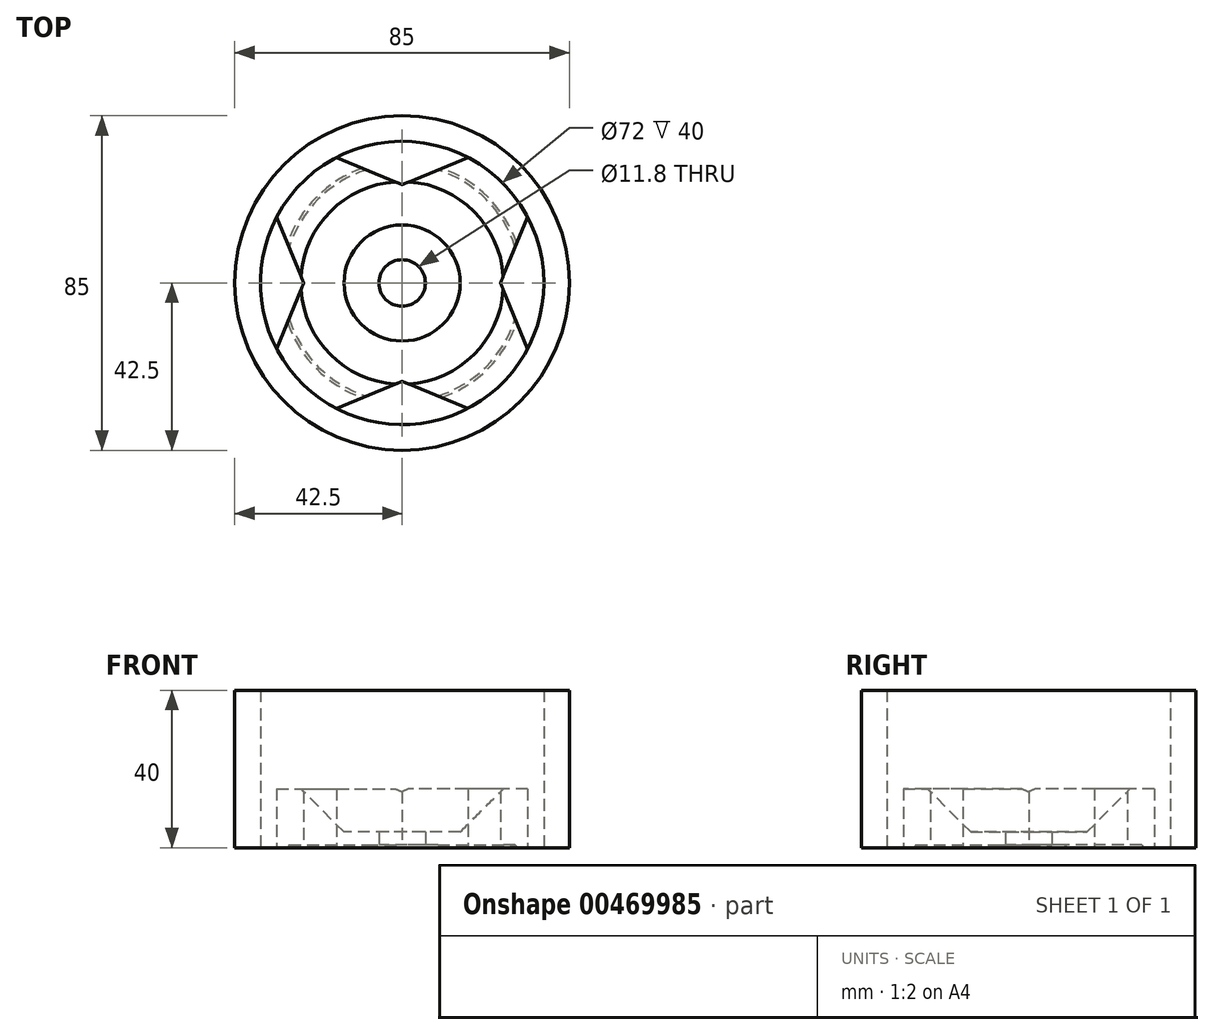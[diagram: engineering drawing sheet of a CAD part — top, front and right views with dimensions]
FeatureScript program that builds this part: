
annotation { "Feature Type Name" : "Feature", "Feature Type Description" : "" }
export const myFeature = defineFeature(function(context is Context, id is Id, definition is map)
    precondition{}
    {
        {
            var Q0;
            Q0=qCreatedBy(makeId("Top.planeOp"),FACE);
            var sketch = newSketch(context, id + "F0", { "sketchPlane" : qUnion([Q0])});
            skCircle(sketch, "E0", {"center": v(0, 0) * mm, "radius": 5.9 * mm});
            skCircle(sketch, "E1", {"center": v(0, 0) * mm, "radius": 11.75 * mm});
            skLineSegment(sketch, "E2.bottom", {"start": v(-42.5, 42.5) * mm, "end": v(42.5, 42.5) * mm, "construction": true});
            skLineSegment(sketch, "E2.top", {"start": v(-42.5, -42.5) * mm, "end": v(42.5, -42.5) * mm, "construction": true});
            skLineSegment(sketch, "E2.left", {"start": v(-42.5, 42.5) * mm, "end": v(-42.5, -42.5) * mm, "construction": true});
            skLineSegment(sketch, "E2.right", {"start": v(42.5, 42.5) * mm, "end": v(42.5, -42.5) * mm, "construction": true});
            skCircle(sketch, "E3.cCircle", {"center": v(0, 0) * mm, "radius": 25 * mm, "construction": true});
            skLineSegment(sketch, "E3.0", {"start": v(-10.35, 25) * mm, "end": v(10.35, 25) * mm, "construction": true});
            skLineSegment(sketch, "E3.1", {"start": v(10.35, 25) * mm, "end": v(25, 10.35) * mm, "construction": true});
            skLineSegment(sketch, "E3.2", {"start": v(25, 10.35) * mm, "end": v(25, -10.35) * mm, "construction": true});
            skLineSegment(sketch, "E3.3", {"start": v(25, -10.35) * mm, "end": v(10.35, -25) * mm, "construction": true});
            skLineSegment(sketch, "E3.4", {"start": v(10.35, -25) * mm, "end": v(-10.35, -25) * mm, "construction": true});
            skLineSegment(sketch, "E3.5", {"start": v(-10.35, -25) * mm, "end": v(-25, -10.35) * mm, "construction": true});
            skLineSegment(sketch, "E3.6", {"start": v(-25, -10.35) * mm, "end": v(-25, 10.35) * mm, "construction": true});
            skLineSegment(sketch, "E3.7", {"start": v(-25, 10.35) * mm, "end": v(-10.35, 25) * mm, "construction": true});
            skPoint(sketch, "E3.0.midPoint", {"position": v(0, 25) * mm});
            skLineSegment(sketch, "E4", {"start": v(-42.5, -42.5) * mm, "end": v(-25, 0) * mm});
            skLineSegment(sketch, "E5", {"start": v(-25, 0) * mm, "end": v(-42.5, 42.5) * mm});
            skLineSegment(sketch, "E6", {"start": v(-42.5, 42.5) * mm, "end": v(0, 25) * mm});
            skLineSegment(sketch, "E7", {"start": v(0, 25) * mm, "end": v(42.5, 42.5) * mm});
            skLineSegment(sketch, "E8", {"start": v(42.5, 42.5) * mm, "end": v(25, 0) * mm});
            skLineSegment(sketch, "E9", {"start": v(25, 0) * mm, "end": v(42.5, -42.5) * mm});
            skLineSegment(sketch, "E10", {"start": v(42.5, -42.5) * mm, "end": v(0, -25) * mm});
            skLineSegment(sketch, "E11", {"start": v(0, -25) * mm, "end": v(-42.5, -42.5) * mm});
            skCircle(sketch, "E12", {"center": v(0, 0) * mm, "radius": 42.5 * mm});
            skCircle(sketch, "E13", {"center": v(0, 0) * mm, "radius": 40 * mm});
            skCircle(sketch, "E14", {"center": v(0, 0) * mm, "radius": 36 * mm});
            skSolve(sketch);
        }
        {
            var Q0;
            {var subQ0=sQuery(id+"F0.wireOp",EDGE,"E12");var subQ1=sQuery(id+"F0.wireOp",EDGE,"E4");var subQ2=makeQuery(id+"F0.imprint","INTERSECT",VERTEX,{"derivedFrom":[subQ1,subQ0]});Q0=makeQuery(id+"F0.imprint","IMPRINT",FACE,{"disambiguationData":[TD([[makeQuery(id+"F0.imprint","IMPRINT",EDGE,{"disambiguationData":[TD([[subQ2,-1.0]])],"derivedFrom":subQ1}),1.0]])]});}
            var Q1;
            {var subQ0=sQuery(id+"F0.wireOp",EDGE,"E12");var subQ1=sQuery(id+"F0.wireOp",EDGE,"E5");var subQ2=makeQuery(id+"F0.imprint","INTERSECT",VERTEX,{"derivedFrom":[subQ1,subQ0]});Q1=makeQuery(id+"F0.imprint","IMPRINT",FACE,{"disambiguationData":[TD([[makeQuery(id+"F0.imprint","IMPRINT",EDGE,{"disambiguationData":[TD([[subQ2,1.0]])],"derivedFrom":subQ1}),-1.0]])]});}
            var Q2;
            {var subQ0=sQuery(id+"F0.wireOp",EDGE,"E12");var subQ1=sQuery(id+"F0.wireOp",EDGE,"E6");var subQ2=makeQuery(id+"F0.imprint","INTERSECT",VERTEX,{"derivedFrom":[subQ1,subQ0]});Q2=makeQuery(id+"F0.imprint","IMPRINT",FACE,{"disambiguationData":[TD([[makeQuery(id+"F0.imprint","IMPRINT",EDGE,{"disambiguationData":[TD([[subQ2,-1.0]])],"derivedFrom":subQ1}),1.0]])]});}
            var Q3;
            {var subQ0=sQuery(id+"F0.wireOp",EDGE,"E12");var subQ1=sQuery(id+"F0.wireOp",EDGE,"E7");var subQ2=makeQuery(id+"F0.imprint","INTERSECT",VERTEX,{"derivedFrom":[subQ1,subQ0]});Q3=makeQuery(id+"F0.imprint","IMPRINT",FACE,{"disambiguationData":[TD([[makeQuery(id+"F0.imprint","IMPRINT",EDGE,{"disambiguationData":[TD([[subQ2,1.0]])],"derivedFrom":subQ1}),-1.0]])]});}
            var Q4;
            {var subQ0=sQuery(id+"F0.wireOp",EDGE,"E12");var subQ1=sQuery(id+"F0.wireOp",EDGE,"E8");var subQ2=makeQuery(id+"F0.imprint","INTERSECT",VERTEX,{"derivedFrom":[subQ1,subQ0]});Q4=makeQuery(id+"F0.imprint","IMPRINT",FACE,{"disambiguationData":[TD([[makeQuery(id+"F0.imprint","IMPRINT",EDGE,{"disambiguationData":[TD([[subQ2,-1.0]])],"derivedFrom":subQ1}),1.0]])]});}
            var Q5;
            {var subQ0=sQuery(id+"F0.wireOp",EDGE,"E12");var subQ1=sQuery(id+"F0.wireOp",EDGE,"E9");var subQ2=makeQuery(id+"F0.imprint","INTERSECT",VERTEX,{"derivedFrom":[subQ1,subQ0]});Q5=makeQuery(id+"F0.imprint","IMPRINT",FACE,{"disambiguationData":[TD([[makeQuery(id+"F0.imprint","IMPRINT",EDGE,{"disambiguationData":[TD([[subQ2,1.0]])],"derivedFrom":subQ1}),-1.0]])]});}
            var Q6;
            {var subQ0=sQuery(id+"F0.wireOp",EDGE,"E12");var subQ1=sQuery(id+"F0.wireOp",EDGE,"E10");var subQ2=makeQuery(id+"F0.imprint","INTERSECT",VERTEX,{"derivedFrom":[subQ1,subQ0]});Q6=makeQuery(id+"F0.imprint","IMPRINT",FACE,{"disambiguationData":[TD([[makeQuery(id+"F0.imprint","IMPRINT",EDGE,{"disambiguationData":[TD([[subQ2,-1.0]])],"derivedFrom":subQ1}),1.0]])]});}
            var Q7;
            {var subQ0=sQuery(id+"F0.wireOp",EDGE,"E12");var subQ1=sQuery(id+"F0.wireOp",EDGE,"E4");var subQ2=makeQuery(id+"F0.imprint","INTERSECT",VERTEX,{"derivedFrom":[subQ1,subQ0]});Q7=makeQuery(id+"F0.imprint","IMPRINT",FACE,{"disambiguationData":[TD([[makeQuery(id+"F0.imprint","IMPRINT",EDGE,{"disambiguationData":[TD([[subQ2,-1.0]])],"derivedFrom":subQ1}),-1.0]])]});}
            var Q8;
            Q8=makeQuery(id+"F0.imprint","IMPRINT",FACE,{"disambiguationData":[TD([[makeQuery(id+"F0.imprint","IMPRINT",EDGE,{"derivedFrom":sQuery(id+"F0.wireOp",EDGE,"E1")}),-1.0]])]});
            var Q9;
            {var subQ0=sQuery(id+"F0.wireOp",EDGE,"E14");var subQ1=sQuery(id+"F0.wireOp",EDGE,"E5");var subQ2=makeQuery(id+"F0.imprint","INTERSECT",VERTEX,{"derivedFrom":[subQ1,subQ0]});Q9=makeQuery(id+"F0.imprint","IMPRINT",FACE,{"disambiguationData":[TD([[makeQuery(id+"F0.imprint","IMPRINT",EDGE,{"disambiguationData":[TD([[subQ2,-1.0]])],"derivedFrom":subQ1}),-1.0]])]});}
            var Q10;
            {var subQ0=sQuery(id+"F0.wireOp",EDGE,"E14");var subQ1=sQuery(id+"F0.wireOp",EDGE,"E7");var subQ2=makeQuery(id+"F0.imprint","INTERSECT",VERTEX,{"derivedFrom":[subQ1,subQ0]});Q10=makeQuery(id+"F0.imprint","IMPRINT",FACE,{"disambiguationData":[TD([[makeQuery(id+"F0.imprint","IMPRINT",EDGE,{"disambiguationData":[TD([[subQ2,-1.0]])],"derivedFrom":subQ1}),-1.0]])]});}
            var Q11;
            {var subQ0=sQuery(id+"F0.wireOp",EDGE,"E13");var subQ1=sQuery(id+"F0.wireOp",EDGE,"E4");var subQ2=makeQuery(id+"F0.imprint","INTERSECT",VERTEX,{"derivedFrom":[subQ1,subQ0]});Q11=makeQuery(id+"F0.imprint","IMPRINT",FACE,{"disambiguationData":[TD([[makeQuery(id+"F0.imprint","IMPRINT",EDGE,{"disambiguationData":[TD([[subQ2,-1.0]])],"derivedFrom":subQ1}),-1.0]])]});}
            var Q12;
            {var subQ0=sQuery(id+"F0.wireOp",EDGE,"E14");var subQ1=sQuery(id+"F0.wireOp",EDGE,"E9");var subQ2=makeQuery(id+"F0.imprint","INTERSECT",VERTEX,{"derivedFrom":[subQ1,subQ0]});Q12=makeQuery(id+"F0.imprint","IMPRINT",FACE,{"disambiguationData":[TD([[makeQuery(id+"F0.imprint","IMPRINT",EDGE,{"disambiguationData":[TD([[subQ2,-1.0]])],"derivedFrom":subQ1}),-1.0]])]});}
            var Q13;
            {var subQ0=sQuery(id+"F0.wireOp",EDGE,"E13");var subQ1=sQuery(id+"F0.wireOp",EDGE,"E4");var subQ2=makeQuery(id+"F0.imprint","INTERSECT",VERTEX,{"derivedFrom":[subQ1,subQ0]});Q13=makeQuery(id+"F0.imprint","IMPRINT",FACE,{"disambiguationData":[TD([[makeQuery(id+"F0.imprint","IMPRINT",EDGE,{"disambiguationData":[TD([[subQ2,-1.0]])],"derivedFrom":subQ1}),1.0]])]});}
            var Q14;
            {var subQ0=sQuery(id+"F0.wireOp",EDGE,"E13");var subQ1=sQuery(id+"F0.wireOp",EDGE,"E6");var subQ2=makeQuery(id+"F0.imprint","INTERSECT",VERTEX,{"derivedFrom":[subQ1,subQ0]});Q14=makeQuery(id+"F0.imprint","IMPRINT",FACE,{"disambiguationData":[TD([[makeQuery(id+"F0.imprint","IMPRINT",EDGE,{"disambiguationData":[TD([[subQ2,-1.0]])],"derivedFrom":subQ1}),1.0]])]});}
            var Q15;
            {var subQ0=sQuery(id+"F0.wireOp",EDGE,"E13");var subQ1=sQuery(id+"F0.wireOp",EDGE,"E8");var subQ2=makeQuery(id+"F0.imprint","INTERSECT",VERTEX,{"derivedFrom":[subQ1,subQ0]});Q15=makeQuery(id+"F0.imprint","IMPRINT",FACE,{"disambiguationData":[TD([[makeQuery(id+"F0.imprint","IMPRINT",EDGE,{"disambiguationData":[TD([[subQ2,-1.0]])],"derivedFrom":subQ1}),1.0]])]});}
            var Q16;
            {var subQ0=sQuery(id+"F0.wireOp",EDGE,"E13");var subQ1=sQuery(id+"F0.wireOp",EDGE,"E10");var subQ2=makeQuery(id+"F0.imprint","INTERSECT",VERTEX,{"derivedFrom":[subQ1,subQ0]});Q16=makeQuery(id+"F0.imprint","IMPRINT",FACE,{"disambiguationData":[TD([[makeQuery(id+"F0.imprint","IMPRINT",EDGE,{"disambiguationData":[TD([[subQ2,-1.0]])],"derivedFrom":subQ1}),1.0]])]});}
            extrude(context, id + "F1", {"entities" : qUnion([Q0, Q1, Q2, Q3, Q4, Q5, Q6, Q7, Q8, Q9, Q10, Q11, Q12, Q13, Q14, Q15, Q16]), "depth" : 40 * mm});
        }
        {
            var Q0;
            Q0=makeQuery(id+"F1.opExtrude","CAP_FACE",FACE,{"disambiguationData":[OSD([sQuery(id+"F0.wireOp",EDGE,"E1"),sQuery(id+"F0.wireOp",EDGE,"E4"),sQuery(id+"F0.wireOp",EDGE,"E5"),sQuery(id+"F0.wireOp",EDGE,"E6"),sQuery(id+"F0.wireOp",EDGE,"E7"),sQuery(id+"F0.wireOp",EDGE,"E8"),sQuery(id+"F0.wireOp",EDGE,"E9"),sQuery(id+"F0.wireOp",EDGE,"E10"),sQuery(id+"F0.wireOp",EDGE,"E11"),sQuery(id+"F0.wireOp",EDGE,"E12"),sQuery(id+"F0.wireOp",EDGE,"E13")])],"isStart":false});
            var sketch = newSketch(context, id + "F2", { "sketchPlane" : qUnion([Q0])});
            skCircle(sketch, "E15", {"center": v(0, 0) * mm, "radius": 36 * mm});
            skSolve(sketch);
        }
        {
            var Q0;
            Q0=qSketchRegion(id+"F2",true);
            extrude(context, id + "F3", {"entities" : qUnion([Q0]), "operationType" : NewBodyOperationType.REMOVE, "oppositeDirection" : true, "depth" : 25 * mm});
        }
        {
            var Q0;
            Q0=makeQuery(id+"F1.opExtrude","CAP_FACE",FACE,{"disambiguationData":[OSD([sQuery(id+"F0.wireOp",EDGE,"E1"),sQuery(id+"F0.wireOp",EDGE,"E4"),sQuery(id+"F0.wireOp",EDGE,"E5"),sQuery(id+"F0.wireOp",EDGE,"E6"),sQuery(id+"F0.wireOp",EDGE,"E7"),sQuery(id+"F0.wireOp",EDGE,"E8"),sQuery(id+"F0.wireOp",EDGE,"E9"),sQuery(id+"F0.wireOp",EDGE,"E10"),sQuery(id+"F0.wireOp",EDGE,"E11"),sQuery(id+"F0.wireOp",EDGE,"E12"),sQuery(id+"F0.wireOp",EDGE,"E14")])],"isStart":true});
            var sketch = newSketch(context, id + "F4", { "sketchPlane" : qUnion([Q0])});
            skCircle(sketch, "E16", {"center": v(0, 0) * mm, "radius": 34.25 * mm});
            skCircle(sketch, "E17.cCircle", {"center": v(0, 0) * mm, "radius": 18.78 * mm, "construction": true});
            skLineSegment(sketch, "E17.0", {"start": v(-18.78, -10.84) * mm, "end": v(-18.78, 10.84) * mm});
            skLineSegment(sketch, "E17.1", {"start": v(-18.78, 10.84) * mm, "end": v(0, 21.69) * mm});
            skLineSegment(sketch, "E17.2", {"start": v(0, 21.69) * mm, "end": v(18.78, 10.84) * mm});
            skLineSegment(sketch, "E17.3", {"start": v(18.78, 10.84) * mm, "end": v(18.78, -10.84) * mm});
            skLineSegment(sketch, "E17.4", {"start": v(18.78, -10.84) * mm, "end": v(0, -21.69) * mm});
            skLineSegment(sketch, "E17.5", {"start": v(0, -21.69) * mm, "end": v(-18.78, -10.84) * mm});
            skPoint(sketch, "E17.0.midPoint", {"position": v(-18.78, 0) * mm});
            skSolve(sketch);
        }
        {
            var Q0;
            Q0=makeQuery(id+"F4.imprint","IMPRINT",FACE,{"disambiguationData":[TD([[makeQuery(id+"F4.imprint","IMPRINT",EDGE,{"derivedFrom":sQuery(id+"F4.wireOp",EDGE,"E17.0")}),1.0]])]});
            extrude(context, id + "F5", {"entities" : qUnion([Q0]), "operationType" : NewBodyOperationType.REMOVE, "oppositeDirection" : true, "depth" : 0.2 * mm});
        }
        {
            var Q0;
            Q0=qCreatedBy(makeId("Top.planeOp"),FACE);
            var sketch = newSketch(context, id + "F6", { "sketchPlane" : qUnion([Q0])});
            skCircle(sketch, "E18", {"center": v(0, 0) * mm, "radius": 11.75 * mm});
            skCircle(sketch, "E19", {"center": v(0, 0) * mm, "radius": 5.9 * mm});
            skSolve(sketch);
        }
        {
            var Q0;
            Q0=makeQuery(id+"F6.imprint","IMPRINT",FACE,{"disambiguationData":[TD([[makeQuery(id+"F6.imprint","IMPRINT",EDGE,{"derivedFrom":sQuery(id+"F6.wireOp",EDGE,"E18")}),1.0]])]});
            extrude(context, id + "F7", {"entities" : qUnion([Q0]), "operationType" : NewBodyOperationType.ADD, "depth" : 4 * mm});
        }
        {
            var Q0;
            Q0=makeQuery(id+"F3.boolean.opBoolean","INTERSECT",EDGE,{"derivedFrom":[makeQuery(id+"F1.opExtrude","SWEPT_FACE",FACE,{"disambiguationData":[OSD([sQuery(id+"F0.wireOp",EDGE,"E1")])]}),makeQuery(id+"F3.opExtrude","CAP_FACE",FACE,{"disambiguationData":[OSD([sQuery(id+"F2.wireOp",EDGE,"E15")])],"isStart":false})]});
            chamfer(context, id + "F8", {"entities" : qUnion([Q0]), "width" : 14 * mm, "tangentPropagation" : true});
        }
        {
            var Q0;
            Q0=qCreatedBy(makeId("Top.planeOp"),FACE);
            var sketch = newSketch(context, id + "F9", { "sketchPlane" : qUnion([Q0])});
            skCircle(sketch, "E20", {"center": v(0, 0) * mm, "radius": 35.12 * mm});
            skSolve(sketch);
        }
        {
            var Q0;
            Q0 = qSketchRegion(id + "F9", true);
            extrude(context, id + "F10", {"entities" : qUnion([Q0]), "operationType" : NewBodyOperationType.REMOVE, "depth" : 0.7 * mm});
        }
        {
            var Q0;
            {var subQ0=sQuery(id+"F9.wireOp",EDGE,"E20");Q0=makeQuery(id+"F10.boolean.opBoolean","COPY",EDGE,{"disambiguationData":[TD([makeQuery(id+"F1.opExtrude","SWEPT_FACE",FACE,{"disambiguationData":[OSD([sQuery(id+"F0.wireOp",EDGE,"E4")])]})])],"derivedFrom":makeQuery(id+"F10.opExtrude","CAP_EDGE",EDGE,{"disambiguationData":[OSD([subQ0])],"isStart":false})});}
            var Q1;
            {var subQ0=sQuery(id+"F9.wireOp",EDGE,"E20");Q1=makeQuery(id+"F10.boolean.opBoolean","COPY",EDGE,{"disambiguationData":[TD([makeQuery(id+"F1.opExtrude","SWEPT_FACE",FACE,{"disambiguationData":[OSD([sQuery(id+"F0.wireOp",EDGE,"E9")])]})])],"derivedFrom":makeQuery(id+"F10.opExtrude","CAP_EDGE",EDGE,{"disambiguationData":[OSD([subQ0])],"isStart":false})});}
            var Q2;
            {var subQ0=sQuery(id+"F9.wireOp",EDGE,"E20");Q2=makeQuery(id+"F10.boolean.opBoolean","COPY",EDGE,{"disambiguationData":[TD([makeQuery(id+"F1.opExtrude","SWEPT_FACE",FACE,{"disambiguationData":[OSD([sQuery(id+"F0.wireOp",EDGE,"E7")])]})])],"derivedFrom":makeQuery(id+"F10.opExtrude","CAP_EDGE",EDGE,{"disambiguationData":[OSD([subQ0])],"isStart":false})});}
            var Q3;
            {var subQ0=sQuery(id+"F9.wireOp",EDGE,"E20");Q3=makeQuery(id+"F10.boolean.opBoolean","COPY",EDGE,{"disambiguationData":[TD([makeQuery(id+"F1.opExtrude","SWEPT_FACE",FACE,{"disambiguationData":[OSD([sQuery(id+"F0.wireOp",EDGE,"E5")])]})])],"derivedFrom":makeQuery(id+"F10.opExtrude","CAP_EDGE",EDGE,{"disambiguationData":[OSD([subQ0])],"isStart":false})});}
            chamfer(context, id + "F11", {"entities" : qUnion([Q0, Q1, Q2, Q3]), "width" : 5 * mm, "tangentPropagation" : true});
        }
    });
